# Revit family: Spoke_Occasional_Tables_BIM
name_source: partatom
category: Arredi
units: mm (PartAtom-declared; Revit-internal decimal feet)

## family parameters
Attiva taglio nelle viste = No
Basato su piano di lavoro = No
Condiviso = No
Numero OmniClass = 23.40.20.00
Origine composizione di rendering = Geometria famiglia
Punto di calcolo locali = No
Sempre verticale = Sì
Taglio con vuoti quando caricato = No
Titolo OmniClass = General Furniture and Specialties

## types (2) — shared parameters
AVAILABLE FINISHES = Ebonized black lacquer on Ash (EB) or bleached, white pigment, matte acrylic on Ash (BL). Raw effect lacquer on Oak (RE). Hand rubbed natural oil on Oak or Walnut (NA), or hand rubbed black oil on Walnut (BO).
BASE MATERIAL = BASSAM_FELLOWS_OAK_O-NA
BIM BADGE = https://bim.archiproducts.com
COLLECTION = Spoke
MATERIAL DESCRIPTION = Sliced solid wood, custom laminated, bent and carved. Low iron glass inset top.
PRODUCT SHEET = https://www.archiproducts.com
Produttore = BassamFellows
TECHNICAL SHEET = https://bassamfellows.com
UPHOLSTERY MATERIAL = BASSAM_FELLOWS_COMFORT_LEATHER_43632_CAMEL
URL = https://bassamfellows.com
zero-valued in all types: Prospetto di default

## per-type parameters (varying)
| type | DIAMETER | Descrizione | HEIGHT | LARGE | Modello | RADIUS | SMALL |
| CB-321 | 500 mm | Round solid wood and glass coffee table

Round solid wood and glass coffee table

Round solid wood and glass coffee table

Round solid wood and glass coffee table

Design ye | 450 mm  [stored 1.47638 ft] | No | Spoke Side Table | 250 mm  [stored 0.82021 ft] | Sì |
| CB-322 | 900 mm | Round solid wood and glass coffee table | 400 mm  [stored 1.31234 ft] | Sì | Spoke Coffee Table | 450 mm  [stored 1.47638 ft] | No |

note: column(s) folded — value = type name in every type: PRODUCT CODE

note: [stored X ft] marks values corroborated as IEEE doubles in the binary element streams (Revit-internal decimal feet)

## geometry (parser evidence)
native form markers: Sweep x2
no freeform markers — native parametric forms only
